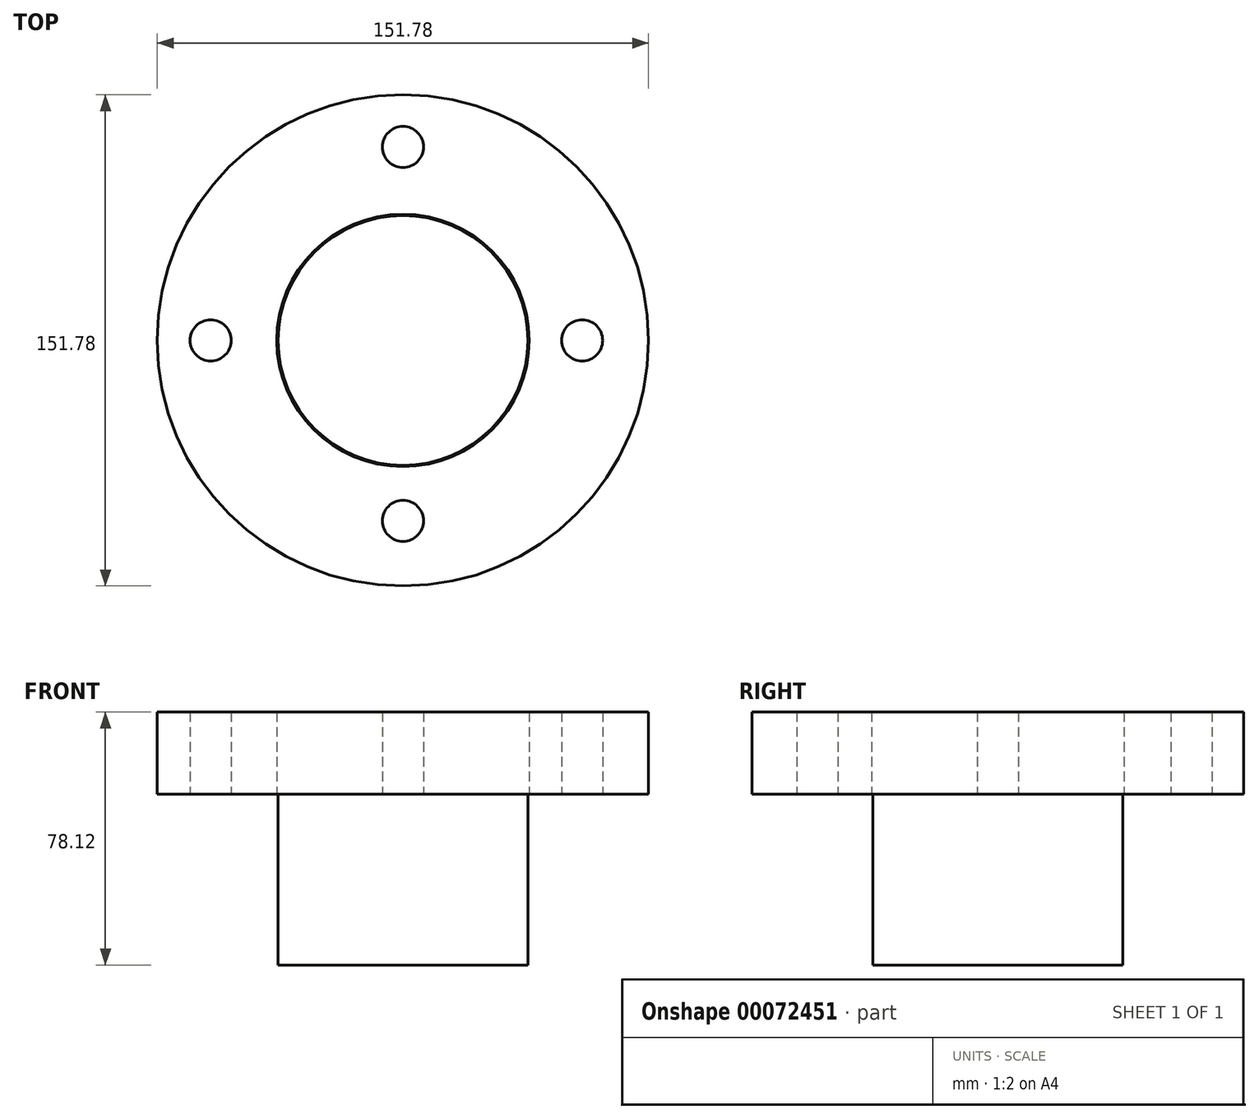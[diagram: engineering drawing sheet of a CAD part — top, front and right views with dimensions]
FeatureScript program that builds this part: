
annotation { "Feature Type Name" : "Feature", "Feature Type Description" : "" }
export const myFeature = defineFeature(function(context is Context, id is Id, definition is map)
    precondition{}
    {
        {
            var Q0;
            Q0=qCreatedBy(makeId("Top.planeOp"),FACE);
            var sketch = newSketch(context, id + "F0", { "sketchPlane" : qUnion([Q0])});
            skCircle(sketch, "E0", {"center": v(0, 0) * mm, "radius": 75.9 * mm});
            skCircle(sketch, "E1", {"center": v(0, 0) * mm, "radius": 39 * mm});
            skCircle(sketch, "E2", {"center": v(0, 59.76) * mm, "radius": 6.35 * mm});
            skCircle(sketch, "E3", {"center": v(-59.41, 0) * mm, "radius": 6.35 * mm});
            skCircle(sketch, "E4", {"center": v(55.35, 0) * mm, "radius": 6.35 * mm});
            skCircle(sketch, "E5", {"center": v(0, -55.76) * mm, "radius": 6.35 * mm});
            skSolve(sketch);
        }
        {
            var Q0;
            Q0=makeQuery(id+"F0.imprint","IMPRINT",FACE,{"disambiguationData":[TD([[makeQuery(id+"F0.imprint","IMPRINT",EDGE,{"derivedFrom":sQuery(id+"F0.wireOp",EDGE,"E0")}),1.0]])]});
            extrude(context, id + "F1", {"entities" : qUnion([Q0]), "depth" : 25.4 * mm});
        }
        {
            var Q0;
            Q0=qCreatedBy(makeId("Top.planeOp"),FACE);
            var sketch = newSketch(context, id + "F2", { "sketchPlane" : qUnion([Q0])});
            skCircle(sketch, "E6", {"center": v(0, 0) * mm, "radius": 38.6 * mm});
            skSolve(sketch);
        }
        {
            var Q0;
            Q0=makeQuery(id+"F2.imprint","IMPRINT",FACE,{"disambiguationData":[TD([[makeQuery(id+"F2.imprint","IMPRINT",EDGE,{"derivedFrom":sQuery(id+"F2.wireOp",EDGE,"E6")}),1.0]])]});
            extrude(context, id + "F3", {"entities" : qUnion([Q0]), "oppositeDirection" : true, "depth" : 52.72 * mm});
        }
    });
